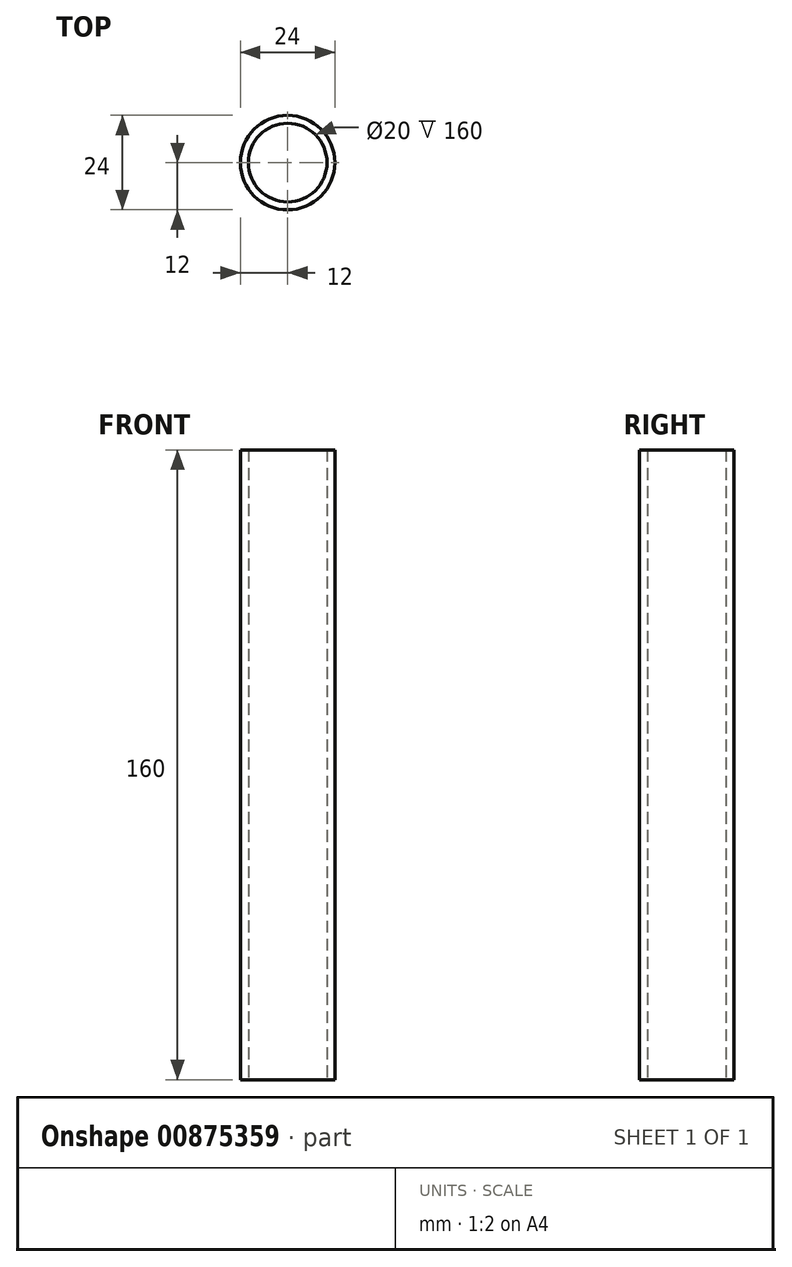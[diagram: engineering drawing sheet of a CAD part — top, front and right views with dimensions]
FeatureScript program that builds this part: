
annotation { "Feature Type Name" : "Feature", "Feature Type Description" : "" }
export const myFeature = defineFeature(function(context is Context, id is Id, definition is map)
    precondition{}
    {
        {
            var Q0;
            Q0=qCreatedBy(makeId("Top.planeOp"),FACE);
            var sketch = newSketch(context, id + "F0", { "sketchPlane" : qUnion([Q0])});
            skCircle(sketch, "E0", {"center": v(0, 0) * mm, "radius": 12 * mm});
            skCircle(sketch, "E1", {"center": v(0, 0) * mm, "radius": 10 * mm});
            skSolve(sketch);
        }
        {
            var Q0;
            Q0 = qSketchRegion(id + "F0", true);
            extrude(context, id + "F1", {"entities" : qUnion([Q0]), "depth" : 160 * mm, "offsetDistance" : 25 * mm});
        }
    });
